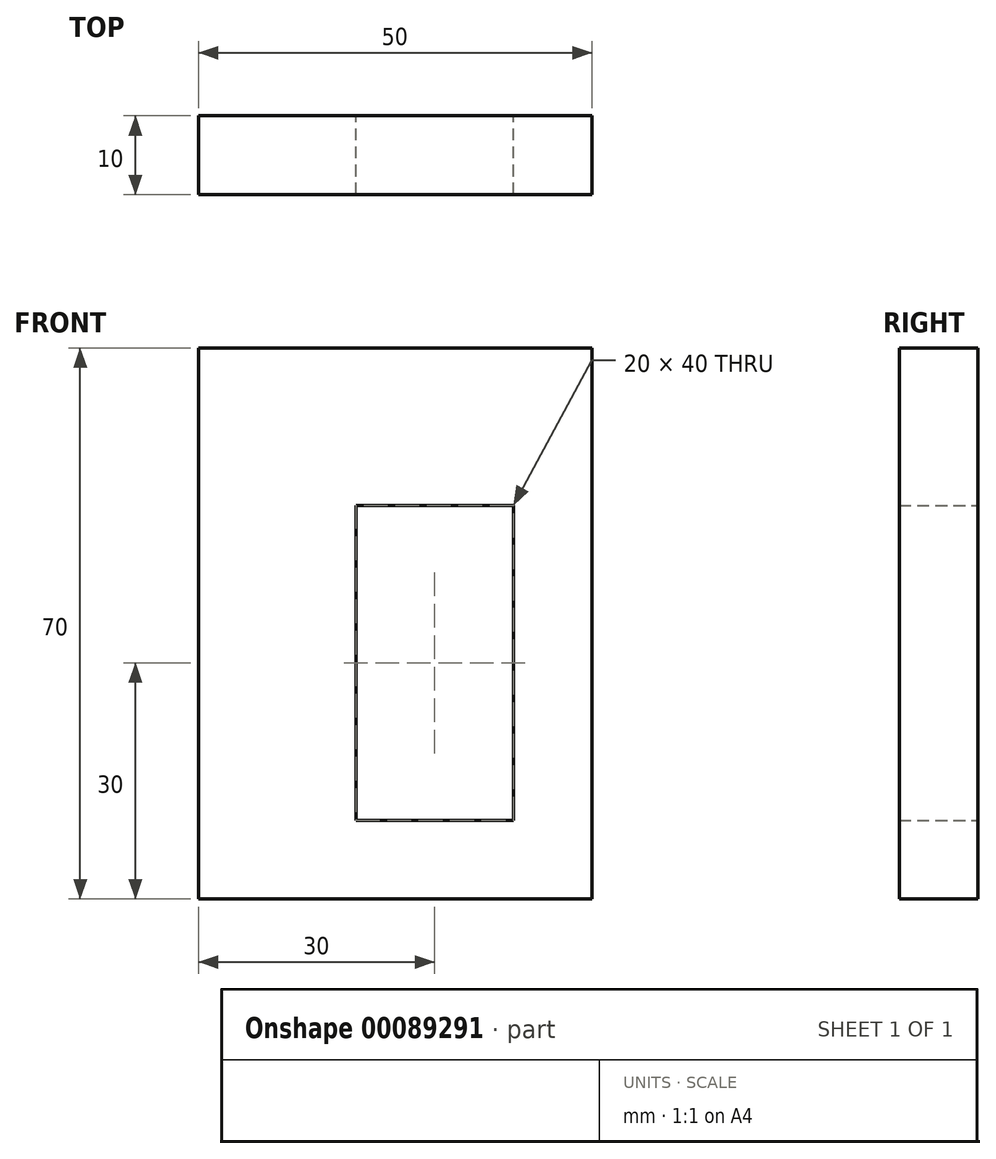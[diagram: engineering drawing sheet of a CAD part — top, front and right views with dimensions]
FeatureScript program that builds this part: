
annotation { "Feature Type Name" : "Feature", "Feature Type Description" : "" }
export const myFeature = defineFeature(function(context is Context, id is Id, definition is map)
    precondition{}
    {
        {
            var Q0;
            Q0=qCreatedBy(makeId("Front.planeOp"),FACE);
            var sketch = newSketch(context, id + "F0", { "sketchPlane" : qUnion([Q0])});
            skLineSegment(sketch, "E0.bottom", {"start": v(0, 0) * mm, "end": v(50, 0) * mm});
            skLineSegment(sketch, "E0.top", {"start": v(0, -70) * mm, "end": v(50, -70) * mm});
            skLineSegment(sketch, "E0.left", {"start": v(0, 0) * mm, "end": v(0, -70) * mm});
            skLineSegment(sketch, "E0.right", {"start": v(50, 0) * mm, "end": v(50, -70) * mm});
            skLineSegment(sketch, "E1.bottom", {"start": v(20, -20) * mm, "end": v(40, -20) * mm});
            skLineSegment(sketch, "E1.top", {"start": v(20, -60) * mm, "end": v(40, -60) * mm});
            skLineSegment(sketch, "E1.left", {"start": v(20, -20) * mm, "end": v(20, -60) * mm});
            skLineSegment(sketch, "E1.right", {"start": v(40, -20) * mm, "end": v(40, -60) * mm});
            skSolve(sketch);
        }
        {
            var Q0;
            Q0 = qSketchRegion(id + "F0", true);
            extrude(context, id + "F1", {"entities" : qUnion([Q0]), "depth" : 10 * mm});
        }
    });
